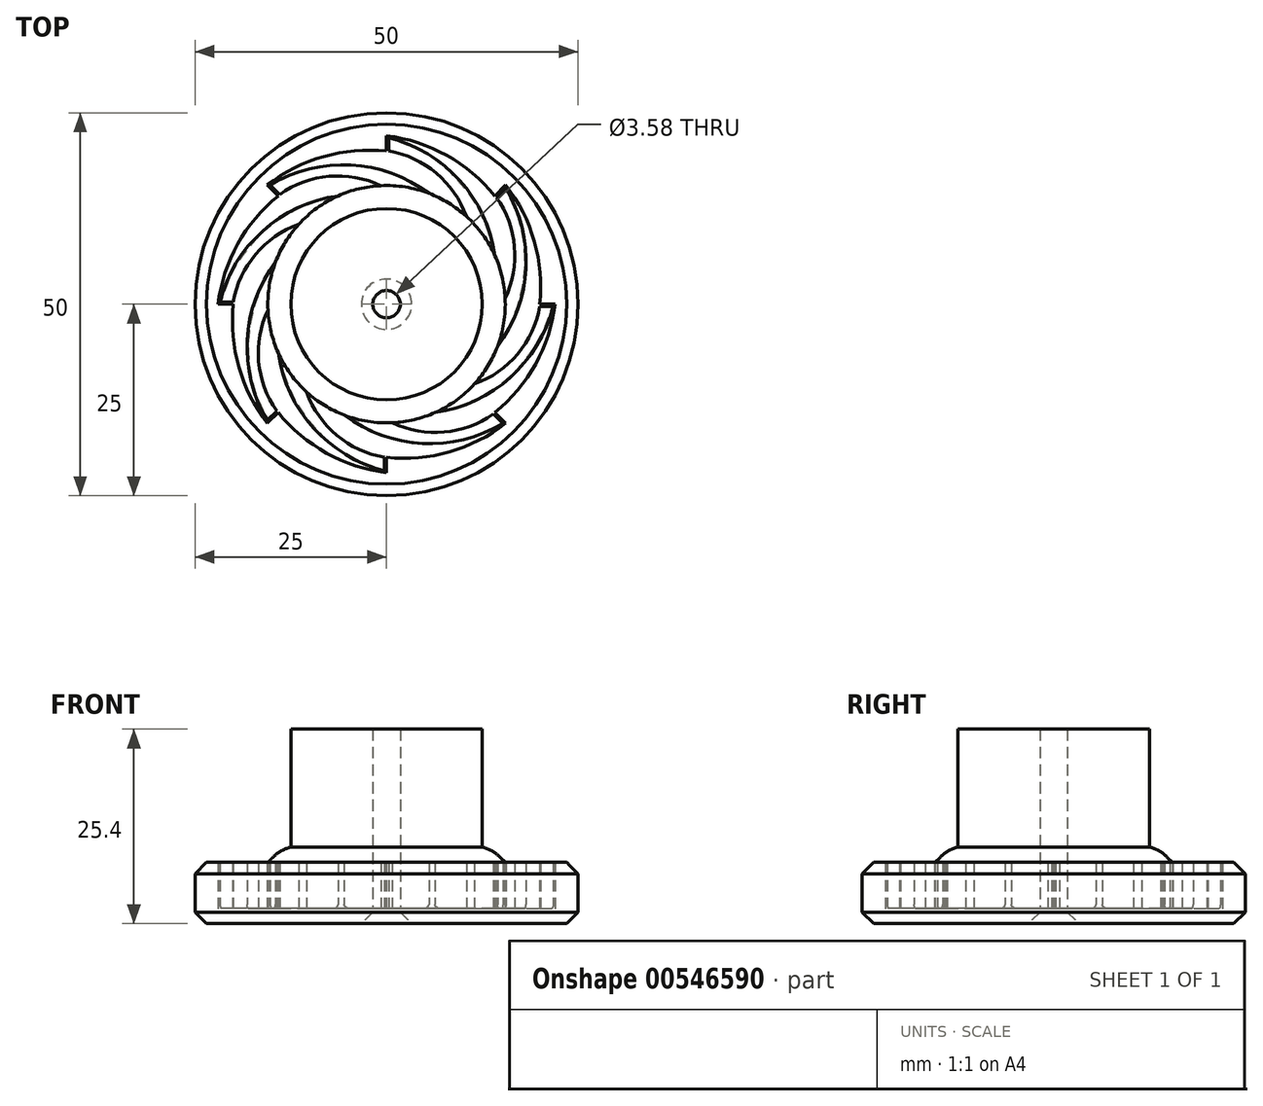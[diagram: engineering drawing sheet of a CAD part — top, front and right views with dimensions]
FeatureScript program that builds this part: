
annotation { "Feature Type Name" : "Feature", "Feature Type Description" : "" }
export const myFeature = defineFeature(function(context is Context, id is Id, definition is map)
    precondition{}
    {
        {
            var Q0;
            Q0=qCreatedBy(makeId("Top.planeOp"),FACE);
            var sketch = newSketch(context, id + "F0", { "sketchPlane" : qUnion([Q0])});
            skCircle(sketch, "E0", {"center": v(0, 0) * mm, "radius": 25 * mm});
            skCircle(sketch, "E1", {"center": v(0, 0) * mm, "radius": 1.8 * mm});
            skArc(sketch, "E2", {"start": v(-0.75, 15.48) * mm, "mid": v(-3.6, 15.08) * mm, "end": v(-6.33, 14.15) * mm});
            skLineSegment(sketch, "E3", {"start": v(0, 25) * mm, "end": v(0, -25) * mm, "construction": true});
            skLineSegment(sketch, "E4", {"start": v(-25, 0) * mm, "end": v(25, 0) * mm, "construction": true});
            skLineSegment(sketch, "E5", {"start": v(-17.68, 17.68) * mm, "end": v(17.68, -17.68) * mm, "construction": true});
            skLineSegment(sketch, "E6", {"start": v(17.68, 17.68) * mm, "end": v(-17.68, -17.68) * mm, "construction": true});
            skArc(sketch, "E7", {"start": v(0, 20) * mm, "mid": v(-8.2, 19.29) * mm, "end": v(-15.56, 15.56) * mm});
            skLineSegment(sketch, "E8", {"start": v(0, 22) * mm, "end": v(0, 20) * mm});
            skLineSegment(sketch, "E9", {"start": v(0.28, 20) * mm, "end": v(0.28, 21.75) * mm});
            skArc(sketch, "E10.1.0", {"start": v(-14.14, 14.14) * mm, "mid": v(-19.44, 7.83) * mm, "end": v(-22, 0) * mm});
            skLineSegment(sketch, "E10.1.1", {"start": v(-15.56, 15.56) * mm, "end": v(-14.14, 14.14) * mm});
            skArc(sketch, "E10.2.0", {"start": v(-20, 0) * mm, "mid": v(-19.29, -8.2) * mm, "end": v(-15.56, -15.56) * mm});
            skLineSegment(sketch, "E10.2.1", {"start": v(-22, 0) * mm, "end": v(-20, 0) * mm});
            skArc(sketch, "E10.3.0", {"start": v(-14.14, -14.14) * mm, "mid": v(-7.83, -19.44) * mm, "end": v(0, -22) * mm});
            skLineSegment(sketch, "E10.3.1", {"start": v(-15.56, -15.56) * mm, "end": v(-14.14, -14.14) * mm});
            skArc(sketch, "E10.4.0", {"start": v(0, -20) * mm, "mid": v(8.2, -19.29) * mm, "end": v(15.56, -15.56) * mm});
            skLineSegment(sketch, "E10.4.1", {"start": v(0, -22) * mm, "end": v(0, -20) * mm});
            skArc(sketch, "E10.5.0", {"start": v(14.14, -14.14) * mm, "mid": v(19.44, -7.83) * mm, "end": v(22, 0) * mm});
            skLineSegment(sketch, "E10.5.1", {"start": v(15.56, -15.56) * mm, "end": v(14.14, -14.14) * mm});
            skArc(sketch, "E10.6.0", {"start": v(20, 0) * mm, "mid": v(19.29, 8.2) * mm, "end": v(15.56, 15.56) * mm});
            skLineSegment(sketch, "E10.6.1", {"start": v(22, 0) * mm, "end": v(20, 0) * mm});
            skArc(sketch, "E10.7.0", {"start": v(14.14, 14.14) * mm, "mid": v(7.83, 19.44) * mm, "end": v(0, 22) * mm});
            skLineSegment(sketch, "E10.7.1", {"start": v(15.56, 15.56) * mm, "end": v(14.14, 14.14) * mm});
            skArc(sketch, "E11", {"start": v(14.15, 6.33) * mm, "mid": v(9.57, 16.16) * mm, "end": v(0.28, 21.75) * mm});
            skArc(sketch, "E12", {"start": v(10.42, 11.48) * mm, "mid": v(6.5, 17.12) * mm, "end": v(0.28, 20) * mm});
            skArc(sketch, "E13.1.0", {"start": v(-0.75, 15.48) * mm, "mid": v(-7.5, 16.7) * mm, "end": v(-13.94, 14.34) * mm});
            skArc(sketch, "E13.1.1", {"start": v(5.53, 14.48) * mm, "mid": v(-4.66, 18.2) * mm, "end": v(-15.18, 15.57) * mm});
            skLineSegment(sketch, "E13.1.2", {"start": v(-13.94, 14.34) * mm, "end": v(-15.18, 15.57) * mm});
            skArc(sketch, "E13.2.0", {"start": v(-11.48, 10.42) * mm, "mid": v(-17.12, 6.5) * mm, "end": v(-20, 0.28) * mm});
            skArc(sketch, "E13.2.1", {"start": v(-6.33, 14.15) * mm, "mid": v(-16.16, 9.57) * mm, "end": v(-21.75, 0.28) * mm});
            skLineSegment(sketch, "E13.2.2", {"start": v(-20, 0.28) * mm, "end": v(-21.75, 0.28) * mm});
            skArc(sketch, "E13.3.0", {"start": v(-15.48, -0.75) * mm, "mid": v(-16.7, -7.5) * mm, "end": v(-14.34, -13.94) * mm});
            skArc(sketch, "E13.3.1", {"start": v(-14.48, 5.53) * mm, "mid": v(-18.2, -4.66) * mm, "end": v(-15.57, -15.18) * mm});
            skLineSegment(sketch, "E13.3.2", {"start": v(-14.34, -13.94) * mm, "end": v(-15.57, -15.18) * mm});
            skArc(sketch, "E13.4.0", {"start": v(-10.42, -11.48) * mm, "mid": v(-6.5, -17.12) * mm, "end": v(-0.28, -20) * mm});
            skArc(sketch, "E13.4.1", {"start": v(-14.15, -6.33) * mm, "mid": v(-9.57, -16.16) * mm, "end": v(-0.28, -21.75) * mm});
            skLineSegment(sketch, "E13.4.2", {"start": v(-0.28, -20) * mm, "end": v(-0.28, -21.75) * mm});
            skArc(sketch, "E13.5.0", {"start": v(0.75, -15.48) * mm, "mid": v(7.5, -16.7) * mm, "end": v(13.94, -14.34) * mm});
            skArc(sketch, "E13.5.1", {"start": v(-5.53, -14.48) * mm, "mid": v(4.66, -18.2) * mm, "end": v(15.18, -15.57) * mm});
            skLineSegment(sketch, "E13.5.2", {"start": v(13.94, -14.34) * mm, "end": v(15.18, -15.57) * mm});
            skArc(sketch, "E13.6.0", {"start": v(11.48, -10.42) * mm, "mid": v(17.12, -6.5) * mm, "end": v(20, -0.28) * mm});
            skArc(sketch, "E13.6.1", {"start": v(6.33, -14.15) * mm, "mid": v(16.16, -9.57) * mm, "end": v(21.75, -0.28) * mm});
            skLineSegment(sketch, "E13.6.2", {"start": v(20, -0.28) * mm, "end": v(21.75, -0.28) * mm});
            skArc(sketch, "E13.7.0", {"start": v(15.48, 0.75) * mm, "mid": v(16.7, 7.5) * mm, "end": v(14.34, 13.94) * mm});
            skArc(sketch, "E13.7.1", {"start": v(14.48, -5.53) * mm, "mid": v(18.2, 4.66) * mm, "end": v(15.57, 15.18) * mm});
            skLineSegment(sketch, "E13.7.2", {"start": v(14.34, 13.94) * mm, "end": v(15.57, 15.18) * mm});
            skArc(sketch, "E14.trimOffspring", {"start": v(10.42, 11.48) * mm, "mid": v(8.11, 13.2) * mm, "end": v(5.53, 14.48) * mm});
            skArc(sketch, "E15.trimOffspring", {"start": v(15.48, 0.75) * mm, "mid": v(15.08, 3.6) * mm, "end": v(14.15, 6.33) * mm});
            skArc(sketch, "E16.trimOffspring", {"start": v(11.48, -10.42) * mm, "mid": v(13.2, -8.11) * mm, "end": v(14.48, -5.53) * mm});
            skArc(sketch, "E17.trimOffspring", {"start": v(-11.48, 10.42) * mm, "mid": v(-13.2, 8.11) * mm, "end": v(-14.48, 5.53) * mm});
            skArc(sketch, "E18.trimOffspring", {"start": v(-15.48, -0.75) * mm, "mid": v(-15.08, -3.6) * mm, "end": v(-14.15, -6.33) * mm});
            skArc(sketch, "E19.trimOffspring", {"start": v(-10.42, -11.48) * mm, "mid": v(-8.11, -13.2) * mm, "end": v(-5.53, -14.48) * mm});
            skArc(sketch, "E20.trimOffspring", {"start": v(0.75, -15.48) * mm, "mid": v(3.6, -15.08) * mm, "end": v(6.33, -14.15) * mm});
            skSolve(sketch);
        }
        {
            var Q0;
            Q0=makeQuery(id+"F0.imprint","IMPRINT",FACE,{"disambiguationData":[TD([[makeQuery(id+"F0.imprint","IMPRINT",EDGE,{"derivedFrom":sQuery(id+"F0.wireOp",EDGE,"E0")}),1.0]])]});
            var Q1;
            Q1=makeQuery(id+"F0.imprint","IMPRINT",FACE,{"disambiguationData":[TD([[makeQuery(id+"F0.imprint","IMPRINT",EDGE,{"derivedFrom":sQuery(id+"F0.wireOp",EDGE,"E2")}),-1.0]])]});
            var Q2;
            Q2=makeQuery(id+"F0.imprint","IMPRINT",FACE,{"disambiguationData":[TD([[makeQuery(id+"F0.imprint","IMPRINT",EDGE,{"derivedFrom":sQuery(id+"F0.wireOp",EDGE,"E1")}),-1.0]])]});
            extrude(context, id + "F1", {"entities" : qUnion([Q0, Q1, Q2]), "oppositeDirection" : true, "depth" : 1.5 * mm});
        }
        {
            var Q0;
            Q0=makeQuery(id+"F0.imprint","IMPRINT",FACE,{"disambiguationData":[TD([[makeQuery(id+"F0.imprint","IMPRINT",EDGE,{"derivedFrom":sQuery(id+"F0.wireOp",EDGE,"E0")}),1.0]])]});
            extrude(context, id + "F2", {"entities" : qUnion([Q0]), "operationType" : NewBodyOperationType.ADD, "depth" : 6.5 * mm});
        }
        {
            var Q0;
            Q0=makeQuery(id+"F0.imprint","IMPRINT",FACE,{"disambiguationData":[TD([[makeQuery(id+"F0.imprint","IMPRINT",EDGE,{"derivedFrom":sQuery(id+"F0.wireOp",EDGE,"E1")}),-1.0]])]});
            var sketch = newSketch(context, id + "F3", { "sketchPlane" : qUnion([Q0])});
            skCircle(sketch, "E21.0", {"center": v(0, 0) * mm, "radius": 1.8 * mm});
            skCircle(sketch, "E22", {"center": v(0, 0) * mm, "radius": 5 * mm});
            skSolve(sketch);
        }
        {
            var Q0;
            Q0=qCreatedBy(makeId("Right.planeOp"),FACE);
            var sketch = newSketch(context, id + "F4", { "sketchPlane" : qUnion([Q0])});
            skLineSegment(sketch, "E23", {"start": v(0, 0) * mm, "end": v(0, 0.5) * mm, "construction": true});
            skLineSegment(sketch, "E24.0", {"start": v(-5, 0) * mm, "end": v(5, 0) * mm});
            skLineSegment(sketch, "E25.0", {"start": v(-1.8, 0) * mm, "end": v(1.8, 0) * mm});
            skLineSegment(sketch, "E26", {"start": v(-1.8, 0) * mm, "end": v(-1.8, 0.5) * mm});
            skLineSegment(sketch, "E27", {"start": v(-5, 0) * mm, "end": v(-1.8, 0.5) * mm});
            skSolve(sketch);
        }
        {
            var Q0;
            {var subQ2=sQuery(id+"F4.wireOp",EDGE,"E26");Q0=makeQuery(id+"F4.imprint","IMPRINT",FACE,{"disambiguationData":[TD([[makeQuery(id+"F4.imprint","IMPRINT",EDGE,{"derivedFrom":subQ2}),1.0]])]});}
            var Q1;
            Q1=sQuery(id+"F4.wireOp",EDGE,"E23");
            revolve(context, id + "F5", {"operationType" : NewBodyOperationType.ADD, "entities" : qUnion([Q0]), "axis" : qUnion([Q1]), "revolveType" : RevolveType.FULL});
        }
        {
            var Q0;
            Q0=makeQuery(id+"F0.imprint","IMPRINT",FACE,{"disambiguationData":[TD([[makeQuery(id+"F0.imprint","IMPRINT",EDGE,{"derivedFrom":sQuery(id+"F0.wireOp",EDGE,"E1")}),-1.0]])]});
            extrude(context, id + "F6", {"entities" : qUnion([Q0]), "depth" : 6.5 * mm});
        }
        {
            var Q0;
            Q0=makeQuery(id+"F6.opExtrude","CAP_FACE",FACE,{"disambiguationData":[OSD([sQuery(id+"F0.wireOp",EDGE,"E1"),sQuery(id+"F0.wireOp",EDGE,"E2"),sQuery(id+"F0.wireOp",EDGE,"E9"),sQuery(id+"F0.wireOp",EDGE,"E11"),sQuery(id+"F0.wireOp",EDGE,"E12"),sQuery(id+"F0.wireOp",EDGE,"E13.1.0"),sQuery(id+"F0.wireOp",EDGE,"E13.1.1"),sQuery(id+"F0.wireOp",EDGE,"E13.1.2"),sQuery(id+"F0.wireOp",EDGE,"E13.2.0"),sQuery(id+"F0.wireOp",EDGE,"E13.2.1"),sQuery(id+"F0.wireOp",EDGE,"E13.2.2"),sQuery(id+"F0.wireOp",EDGE,"E13.3.0"),sQuery(id+"F0.wireOp",EDGE,"E13.3.1"),sQuery(id+"F0.wireOp",EDGE,"E13.3.2"),sQuery(id+"F0.wireOp",EDGE,"E13.4.0"),sQuery(id+"F0.wireOp",EDGE,"E13.4.1"),sQuery(id+"F0.wireOp",EDGE,"E13.4.2"),sQuery(id+"F0.wireOp",EDGE,"E13.5.0"),sQuery(id+"F0.wireOp",EDGE,"E13.5.1"),sQuery(id+"F0.wireOp",EDGE,"E13.5.2"),sQuery(id+"F0.wireOp",EDGE,"E13.6.0"),sQuery(id+"F0.wireOp",EDGE,"E13.6.1"),sQuery(id+"F0.wireOp",EDGE,"E13.6.2"),sQuery(id+"F0.wireOp",EDGE,"E13.7.0"),sQuery(id+"F0.wireOp",EDGE,"E13.7.1"),sQuery(id+"F0.wireOp",EDGE,"E13.7.2"),sQuery(id+"F0.wireOp",EDGE,"E14.trimOffspring"),sQuery(id+"F0.wireOp",EDGE,"E15.trimOffspring"),sQuery(id+"F0.wireOp",EDGE,"E16.trimOffspring"),sQuery(id+"F0.wireOp",EDGE,"E17.trimOffspring"),sQuery(id+"F0.wireOp",EDGE,"E18.trimOffspring"),sQuery(id+"F0.wireOp",EDGE,"E19.trimOffspring"),sQuery(id+"F0.wireOp",EDGE,"E20.trimOffspring")])],"isStart":false});
            var sketch = newSketch(context, id + "F7", { "sketchPlane" : qUnion([Q0])});
            skCircle(sketch, "E28.0", {"center": v(0, 0) * mm, "radius": 1.8 * mm});
            skCircle(sketch, "E29", {"center": v(0, 0) * mm, "radius": 15.5 * mm});
            skCircle(sketch, "E30", {"center": v(0, 0) * mm, "radius": 12.5 * mm});
            skSolve(sketch);
        }
        {
            var Q0;
            Q0=makeQuery(id+"F7.imprint","IMPRINT",FACE,{"disambiguationData":[TD([[makeQuery(id+"F7.imprint","IMPRINT",EDGE,{"derivedFrom":sQuery(id+"F7.wireOp",EDGE,"E28.0")}),-1.0]])]});
            extrude(context, id + "F8", {"entities" : qUnion([Q0]), "operationType" : NewBodyOperationType.ADD, "depth" : 17.4 * mm});
        }
        {
            var Q0;
            Q0=makeQuery(id+"F7.imprint","IMPRINT",FACE,{"disambiguationData":[TD([[makeQuery(id+"F7.imprint","IMPRINT",EDGE,{"derivedFrom":sQuery(id+"F7.wireOp",EDGE,"E30")}),-1.0]])]});
            extrude(context, id + "F9", {"entities" : qUnion([Q0]), "operationType" : NewBodyOperationType.ADD, "depth" : 2 * mm});
        }
        {
            var Q0;
            Q0=makeQuery(id+"F9.opExtrude","CAP_EDGE",EDGE,{"disambiguationData":[OSD([sQuery(id+"F7.wireOp",EDGE,"E29")])],"isStart":false});
            chamfer(context, id + "F10", {"entities" : qUnion([Q0]), "width" : 2 * mm, "tangentPropagation" : true});
        }
        {
            var Q0;
            {var subQ0=sQuery(id+"F7.wireOp",EDGE,"E29");Q0=makeQuery(id+"F10.opChamfer","BLEND_EDGE",EDGE,{"blendedFrom":[makeQuery(id+"F9.opExtrude","CAP_EDGE",EDGE,{"disambiguationData":[OSD([subQ0])],"isStart":false}),makeQuery(id+"F9.opExtrude","CAP_FACE",FACE,{"disambiguationData":[OSD([subQ0,sQuery(id+"F7.wireOp",EDGE,"E30")])],"isStart":false})],"blendedInto":[makeQuery(id+"F9.opExtrude","CAP_FACE",FACE,{"disambiguationData":[OSD([subQ0,sQuery(id+"F7.wireOp",EDGE,"E30")])],"isStart":false})]});}
            fillet(context, id + "F11", {"entities" : qUnion([Q0]), "radius" : 5 * mm, "tangentPropagation" : true, "allowEdgeOverflow" : false});
        }
        {
            var Q0;
            Q0=makeQuery(id+"FRPSkxED9zWS2Au_2.opExtrude","CAP_EDGE",EDGE,{"disambiguationData":[OSD([sQuery(id+"FCk0wZXI9kaQeSw_2.wireOp",EDGE,"b51c547b-5c0a-4784-866c-d3d9e6590edd.0")])],"isStart":true});
            var Q1;
            Q1=makeQuery(id+"F2.opExtrude","CAP_EDGE",EDGE,{"disambiguationData":[OSD([sQuery(id+"F0.wireOp",EDGE,"E0")])],"isStart":false});
            var Q2;
            Q2=makeQuery(id+"F1.opExtrude","CAP_FACE",FACE,{"disambiguationData":[OSD([sQuery(id+"F0.wireOp",EDGE,"E0"),sQuery(id+"F0.wireOp",EDGE,"E1")])],"isStart":false});
            chamfer(context, id + "F12", {"entities" : qUnion([Q0, Q1, Q2]), "width" : 1.5 * mm, "tangentPropagation" : true});
        }
        {
            var Q0;
            Q0=makeQuery(id+"F1.opExtrude","CAP_EDGE",EDGE,{"disambiguationData":[OSD([sQuery(id+"F0.wireOp",EDGE,"E0")])],"isStart":false});
            var Q1;
            Q1=makeQuery(id+"F2.opExtrude","CAP_EDGE",EDGE,{"disambiguationData":[OSD([sQuery(id+"F0.wireOp",EDGE,"E0")])],"isStart":false});
            var Q2;
            Q2=makeQuery(id+"F6.opExtrude","CAP_EDGE",EDGE,{"disambiguationData":[OSD([sQuery(id+"F0.wireOp",EDGE,"E13.4.1")])],"isStart":true});
            var Q3;
            Q3=makeQuery(id+"F6.opExtrude","CAP_EDGE",EDGE,{"disambiguationData":[OSD([sQuery(id+"F0.wireOp",EDGE,"E13.3.1")])],"isStart":true});
            var Q4;
            Q4=makeQuery(id+"F6.opExtrude","CAP_EDGE",EDGE,{"disambiguationData":[OSD([sQuery(id+"F0.wireOp",EDGE,"E13.2.1")])],"isStart":true});
            var Q5;
            Q5=makeQuery(id+"F6.opExtrude","CAP_EDGE",EDGE,{"disambiguationData":[OSD([sQuery(id+"F0.wireOp",EDGE,"E13.1.1")])],"isStart":true});
            var Q6;
            Q6=makeQuery(id+"F6.opExtrude","CAP_EDGE",EDGE,{"disambiguationData":[OSD([sQuery(id+"F0.wireOp",EDGE,"E11")])],"isStart":true});
            var Q7;
            Q7=makeQuery(id+"F6.opExtrude","CAP_EDGE",EDGE,{"disambiguationData":[OSD([sQuery(id+"F0.wireOp",EDGE,"E13.7.1")])],"isStart":true});
            var Q8;
            Q8=makeQuery(id+"F6.opExtrude","CAP_EDGE",EDGE,{"disambiguationData":[OSD([sQuery(id+"F0.wireOp",EDGE,"E13.6.1")])],"isStart":true});
            var Q9;
            Q9=makeQuery(id+"F6.opExtrude","CAP_EDGE",EDGE,{"disambiguationData":[OSD([sQuery(id+"F0.wireOp",EDGE,"E13.5.1")])],"isStart":true});
            fillet(context, id + "F13", {"entities" : qUnion([Q0, Q1, Q2, Q3, Q4, Q5, Q6, Q7, Q8, Q9]), "radius" : 1 * mm, "tangentPropagation" : true, "allowEdgeOverflow" : false});
        }
        {
            var Q0;
            Q0=makeQuery(id+"F0.imprint","IMPRINT",FACE,{"disambiguationData":[TD([[makeQuery(id+"F0.imprint","IMPRINT",EDGE,{"derivedFrom":sQuery(id+"F0.wireOp",EDGE,"E1")}),-1.0]])]});
            extrude(context, id + "F14", {"entities" : qUnion([Q0]), "operationType" : NewBodyOperationType.REMOVE, "depth" : .5 * mm});
        }
    });
